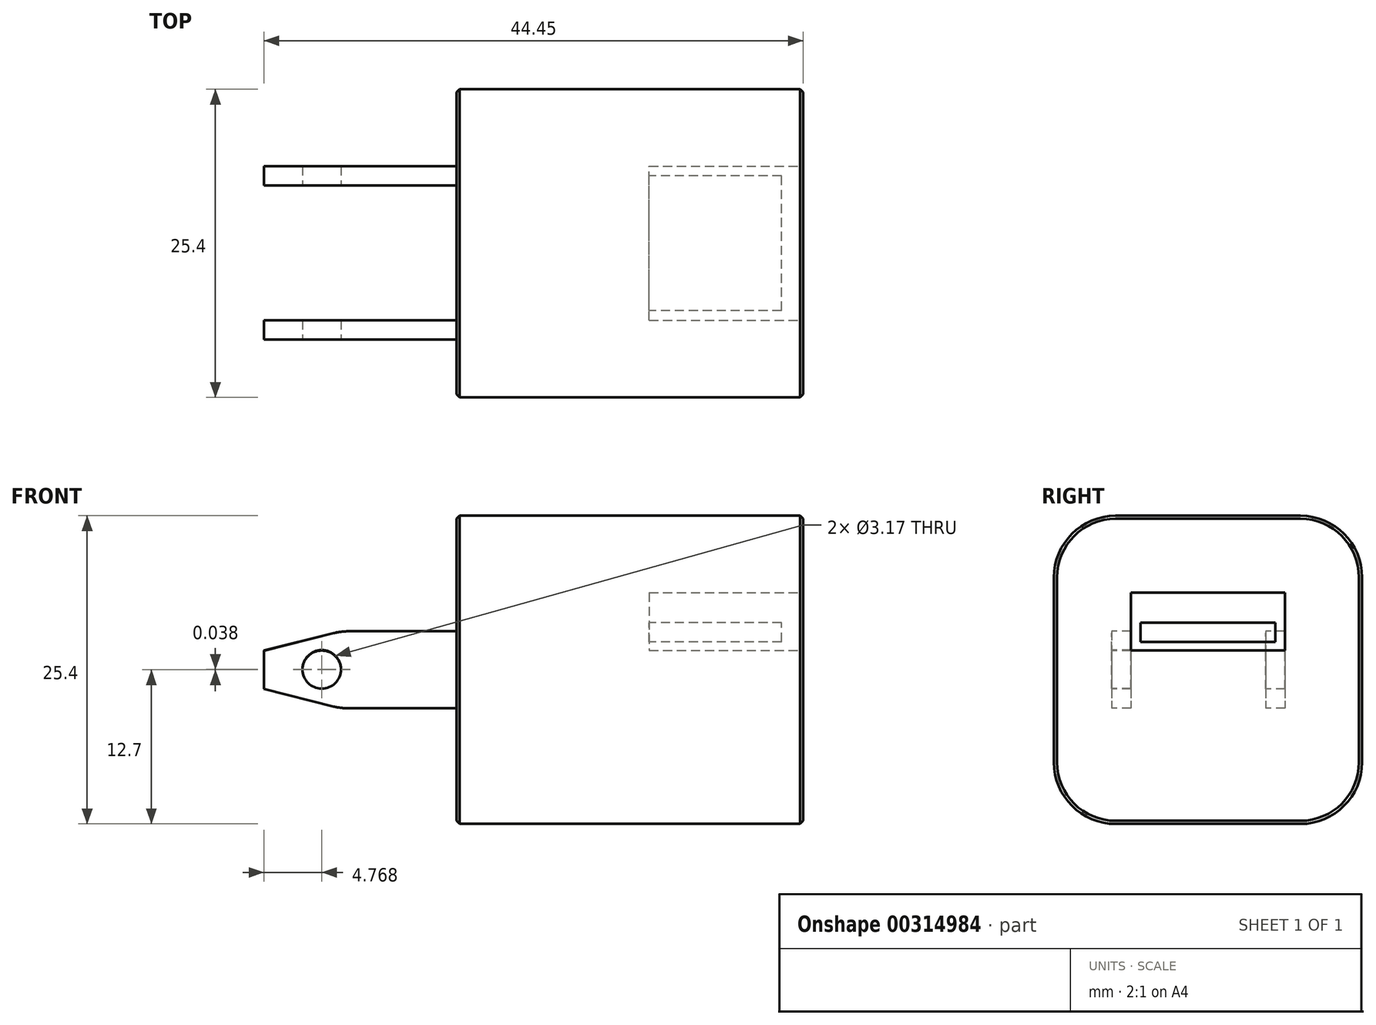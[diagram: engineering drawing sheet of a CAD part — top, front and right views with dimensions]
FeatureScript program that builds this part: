
annotation { "Feature Type Name" : "Feature", "Feature Type Description" : "" }
export const myFeature = defineFeature(function(context is Context, id is Id, definition is map)
    precondition{}
    {
        {
            var Q0;
            Q0=qCreatedBy(makeId("Top.planeOp"),FACE);
            var sketch = newSketch(context, id + "F0", { "sketchPlane" : qUnion([Q0])});
            skLineSegment(sketch, "E0", {"start": v(0, 0) * mm, "end": v(28.58, 0) * mm});
            skLineSegment(sketch, "E1", {"start": v(28.58, 0) * mm, "end": v(28.58, -25.4) * mm});
            skLineSegment(sketch, "E2", {"start": v(0, 0) * mm, "end": v(0, -25.4) * mm});
            skLineSegment(sketch, "E3", {"start": v(0, -25.4) * mm, "end": v(28.58, -25.4) * mm});
            skSolve(sketch);
        }
        {
            var Q0;
            Q0=makeQuery(id+"F0.imprint","IMPRINT",FACE,{"disambiguationData":[TD([[makeQuery(id+"F0.imprint","IMPRINT",EDGE,{"derivedFrom":sQuery(id+"F0.wireOp",EDGE,"E0")}),-1.0]])]});
            extrude(context, id + "F1", {"entities" : qUnion([Q0]), "depth" : 25.4 * mm});
        }
        {
            var Q0;
            Q0=makeQuery(id+"F1.opExtrude","CAP_EDGE",EDGE,{"disambiguationData":[OSD([sQuery(id+"F0.wireOp",EDGE,"E3")])],"isStart":false});
            var Q1;
            Q1=makeQuery(id+"F1.opExtrude","CAP_EDGE",EDGE,{"disambiguationData":[OSD([sQuery(id+"F0.wireOp",EDGE,"E0")])],"isStart":false});
            var Q2;
            Q2=makeQuery(id+"F1.opExtrude","CAP_EDGE",EDGE,{"disambiguationData":[OSD([sQuery(id+"F0.wireOp",EDGE,"E3")])],"isStart":true});
            var Q3;
            Q3=makeQuery(id+"F1.opExtrude","CAP_EDGE",EDGE,{"disambiguationData":[OSD([sQuery(id+"F0.wireOp",EDGE,"E0")])],"isStart":true});
            fillet(context, id + "F2", {"entities" : qUnion([Q0, Q1, Q2, Q3]), "radius" : 5.08 * mm, "tangentPropagation" : true, "allowEdgeOverflow" : false});
        }
        {
            var Q0;
            Q0=makeQuery(id+"F1.opExtrude","SWEPT_FACE",FACE,{"disambiguationData":[OSD([sQuery(id+"F0.wireOp",EDGE,"E1")])]});
            var sketch = newSketch(context, id + "F3", { "sketchPlane" : qUnion([Q0])});
            skLineSegment(sketch, "E4", {"start": v(-19.05, 19.05) * mm, "end": v(-6.35, 19.05) * mm});
            skLineSegment(sketch, "E5", {"start": v(-19.05, 19.05) * mm, "end": v(-19.05, 14.29) * mm});
            skLineSegment(sketch, "E6", {"start": v(-19.05, 14.29) * mm, "end": v(-6.35, 14.29) * mm});
            skLineSegment(sketch, "E7", {"start": v(-6.35, 14.29) * mm, "end": v(-6.35, 19.05) * mm});
            skSolve(sketch);
        }
        {
            var Q0;
            Q0 = qSketchRegion(id + "F3", true);
            extrude(context, id + "F4", {"entities" : qUnion([Q0]), "operationType" : NewBodyOperationType.REMOVE, "oppositeDirection" : true, "depth" : 12.7 * mm});
        }
        {
            var Q0;
            Q0=makeQuery(id+"F4.boolean.opBoolean","COPY",FACE,{"derivedFrom":makeQuery(id+"F4.opExtrude","CAP_FACE",FACE,{"disambiguationData":[OSD([sQuery(id+"F3.wireOp",EDGE,"E4"),sQuery(id+"F3.wireOp",EDGE,"E5"),sQuery(id+"F3.wireOp",EDGE,"E6"),sQuery(id+"F3.wireOp",EDGE,"E7")])],"isStart":false})});
            var sketch = newSketch(context, id + "F5", { "sketchPlane" : qUnion([Q0])});
            skLineSegment(sketch, "E8", {"start": v(-18.25, 15.01) * mm, "end": v(-7.14, 15.01) * mm});
            skLineSegment(sketch, "E9", {"start": v(-7.14, 15.01) * mm, "end": v(-7.14, 16.6) * mm});
            skLineSegment(sketch, "E10", {"start": v(-18.25, 15.01) * mm, "end": v(-18.25, 16.6) * mm});
            skLineSegment(sketch, "E11", {"start": v(-18.25, 16.6) * mm, "end": v(-7.14, 16.6) * mm});
            skSolve(sketch);
        }
        {
            var Q0;
            Q0=makeQuery(id+"F5.imprint","IMPRINT",FACE,{"disambiguationData":[TD([[makeQuery(id+"F5.imprint","IMPRINT",EDGE,{"derivedFrom":sQuery(id+"F5.wireOp",EDGE,"E8")}),1.0]])]});
            extrude(context, id + "F6", {"entities" : qUnion([Q0]), "operationType" : NewBodyOperationType.ADD, "depth" : 10.92 * mm});
        }
        {
            var Q0;
            Q0=makeQuery(id+"F1.opExtrude","SWEPT_FACE",FACE,{"disambiguationData":[OSD([sQuery(id+"F0.wireOp",EDGE,"E2")])]});
            var sketch = newSketch(context, id + "F7", { "sketchPlane" : qUnion([Q0])});
            skLineSegment(sketch, "E12", {"start": v(19.05, 15.88) * mm, "end": v(20.64, 15.88) * mm});
            skLineSegment(sketch, "E13", {"start": v(19.05, 15.88) * mm, "end": v(19.05, 9.53) * mm});
            skLineSegment(sketch, "E14", {"start": v(19.05, 9.53) * mm, "end": v(20.64, 9.53) * mm});
            skLineSegment(sketch, "E15", {"start": v(20.64, 15.88) * mm, "end": v(20.64, 9.53) * mm});
            skSolve(sketch);
        }
        {
            var Q0;
            Q0=makeQuery(id+"F7.imprint","IMPRINT",FACE,{"disambiguationData":[TD([[makeQuery(id+"F7.imprint","IMPRINT",EDGE,{"derivedFrom":sQuery(id+"F7.wireOp",EDGE,"E12")}),-1.0]])]});
            extrude(context, id + "F8", {"entities" : qUnion([Q0]), "operationType" : NewBodyOperationType.ADD, "depth" : 9.52 * mm});
        }
        {
            var Q0;
            Q0=makeQuery(id+"F8.opExtrude","SWEPT_FACE",FACE,{"disambiguationData":[OSD([sQuery(id+"F7.wireOp",EDGE,"E15")])]});
            var sketch = newSketch(context, id + "F9", { "sketchPlane" : qUnion([Q0])});
            skLineSegment(sketch, "E16", {"start": v(-9.53, 9.53) * mm, "end": v(-9.53, 11.11) * mm});
            skLineSegment(sketch, "E17", {"start": v(-9.53, 11.11) * mm, "end": v(-15.88, 11.11) * mm});
            skLineSegment(sketch, "E18", {"start": v(-15.88, 11.11) * mm, "end": v(-9.53, 9.53) * mm});
            skLineSegment(sketch, "E19", {"start": v(-9.53, 15.88) * mm, "end": v(-9.53, 14.27) * mm});
            skLineSegment(sketch, "E20", {"start": v(-9.53, 14.27) * mm, "end": v(-15.88, 14.27) * mm});
            skLineSegment(sketch, "E21", {"start": v(-15.88, 14.27) * mm, "end": v(-9.53, 15.88) * mm});
            skLineSegment(sketch, "E22", {"start": v(-15.88, 14.27) * mm, "end": v(-15.88, 11.11) * mm});
            skLineSegment(sketch, "E23", {"start": v(-9.53, 14.27) * mm, "end": v(-9.53, 11.11) * mm});
            skSolve(sketch);
        }
        {
            var Q0;
            Q0 = qSketchRegion(id + "F9", true);
            extrude(context, id + "F10", {"entities" : qUnion([Q0]), "operationType" : NewBodyOperationType.ADD, "oppositeDirection" : true, "depth" : 1.59 * mm});
        }
        {
            var Q0;
            Q0=makeQuery(id+"F10.boolean.opBoolean","MERGE",FACE,{"derivedFrom":[makeQuery(id+"F8.opExtrude","SWEPT_FACE",FACE,{"disambiguationData":[OSD([sQuery(id+"F7.wireOp",EDGE,"E15")])]}),makeQuery(id+"F10.opExtrude","CAP_FACE",FACE,{"disambiguationData":[OSD([sQuery(id+"F9.wireOp",EDGE,"E16"),sQuery(id+"F9.wireOp",EDGE,"E18"),sQuery(id+"F9.wireOp",EDGE,"E19"),sQuery(id+"F9.wireOp",EDGE,"E21"),sQuery(id+"F9.wireOp",EDGE,"E22"),sQuery(id+"F9.wireOp",EDGE,"E23")])],"isStart":true})]});
            var sketch = newSketch(context, id + "F11", { "sketchPlane" : qUnion([Q0])});
            skCircle(sketch, "E24", {"center": v(-11.11, 12.74) * mm, "radius": 1.59 * mm});
            skSolve(sketch);
        }
        {
            var Q0;
            Q0=makeQuery(id+"F11.imprint","IMPRINT",FACE,{"disambiguationData":[TD([[makeQuery(id+"F11.imprint","IMPRINT",EDGE,{"derivedFrom":sQuery(id+"F11.wireOp",EDGE,"E24")}),1.0]])]});
            extrude(context, id + "F12", {"entities" : qUnion([Q0]), "operationType" : NewBodyOperationType.REMOVE, "oppositeDirection" : true, "depth" : 1.59 * mm});
        }
        {
            var Q0;
            {var subQ0=sQuery(id+"F7.wireOp",EDGE,"E12");Q0=makeQuery(id+"F10.boolean.opBoolean","MERGE",EDGE,{"derivedFrom":[makeQuery(id+"F8.opExtrude","CAP_EDGE",EDGE,{"disambiguationData":[OSD([subQ0])],"isStart":false}),makeQuery(id+"F10.opExtrude","SWEPT_EDGE",EDGE,{"disambiguationData":[OSD([subQ0,sQuery(id+"F7.wireOp",EDGE,"E15"),sQuery(id+"F9.wireOp",EDGE,"E19"),sQuery(id+"F9.wireOp",EDGE,"E21")])]})]});}
            var Q1;
            {var subQ0=sQuery(id+"F7.wireOp",EDGE,"E14");Q1=makeQuery(id+"F10.boolean.opBoolean","MERGE",EDGE,{"derivedFrom":[makeQuery(id+"F8.opExtrude","CAP_EDGE",EDGE,{"disambiguationData":[OSD([subQ0])],"isStart":false}),makeQuery(id+"F10.opExtrude","SWEPT_EDGE",EDGE,{"disambiguationData":[OSD([subQ0,sQuery(id+"F7.wireOp",EDGE,"E15"),sQuery(id+"F9.wireOp",EDGE,"E16"),sQuery(id+"F9.wireOp",EDGE,"E18")])]})]});}
            fillet(context, id + "F13", {"entities" : qUnion([Q0, Q1]), "radius" : 5.08 * mm, "tangentPropagation" : true, "allowEdgeOverflow" : false});
        }
        {
            var Q0;
            Q0=makeQuery(id+"F1.opExtrude","SWEPT_FACE",FACE,{"disambiguationData":[OSD([sQuery(id+"F0.wireOp",EDGE,"E2")])]});
            var sketch = newSketch(context, id + "F14", { "sketchPlane" : qUnion([Q0])});
            skLineSegment(sketch, "E25", {"start": v(6.35, 15.88) * mm, "end": v(7.94, 15.88) * mm});
            skLineSegment(sketch, "E26", {"start": v(6.35, 9.53) * mm, "end": v(7.94, 9.53) * mm});
            skLineSegment(sketch, "E27", {"start": v(6.35, 15.88) * mm, "end": v(6.35, 9.53) * mm});
            skLineSegment(sketch, "E28", {"start": v(7.94, 15.88) * mm, "end": v(7.94, 9.53) * mm});
            skSolve(sketch);
        }
        {
            var Q0;
            Q0=makeQuery(id+"F14.imprint","IMPRINT",FACE,{"disambiguationData":[TD([[makeQuery(id+"F14.imprint","IMPRINT",EDGE,{"derivedFrom":sQuery(id+"F14.wireOp",EDGE,"E25")}),-1.0]])]});
            extrude(context, id + "F15", {"entities" : qUnion([Q0]), "operationType" : NewBodyOperationType.ADD, "depth" : 9.52 * mm});
        }
        {
            var Q0;
            Q0=makeQuery(id+"F15.opExtrude","SWEPT_FACE",FACE,{"disambiguationData":[OSD([sQuery(id+"F14.wireOp",EDGE,"E28")])]});
            var sketch = newSketch(context, id + "F16", { "sketchPlane" : qUnion([Q0])});
            skLineSegment(sketch, "E29", {"start": v(-9.53, 15.88) * mm, "end": v(-9.53, 14.29) * mm});
            skLineSegment(sketch, "E30", {"start": v(-9.53, 14.29) * mm, "end": v(-15.88, 14.29) * mm});
            skLineSegment(sketch, "E31", {"start": v(-15.88, 14.29) * mm, "end": v(-9.53, 15.88) * mm});
            skLineSegment(sketch, "E32", {"start": v(-9.53, 9.53) * mm, "end": v(-9.53, 11.11) * mm});
            skLineSegment(sketch, "E33", {"start": v(-9.53, 11.11) * mm, "end": v(-15.88, 11.11) * mm});
            skLineSegment(sketch, "E34", {"start": v(-15.88, 11.11) * mm, "end": v(-9.53, 9.53) * mm});
            skLineSegment(sketch, "E35", {"start": v(-15.88, 14.29) * mm, "end": v(-15.88, 11.11) * mm});
            skSolve(sketch);
        }
        {
            var Q0;
            {var subQ0=sQuery(id+"F16.wireOp",EDGE,"E30");Q0=makeQuery(id+"F16.imprint","IMPRINT",FACE,{"disambiguationData":[TD([[makeQuery(id+"F16.imprint","IMPRINT",EDGE,{"derivedFrom":subQ0}),1.0]])]});}
            var Q1;
            Q1=makeQuery(id+"F16.imprint","IMPRINT",FACE,{"disambiguationData":[TD([[makeQuery(id+"F16.imprint","IMPRINT",EDGE,{"derivedFrom":sQuery(id+"F16.wireOp",EDGE,"E29")}),-1.0]])]});
            var Q2;
            Q2=makeQuery(id+"F16.imprint","IMPRINT",FACE,{"disambiguationData":[TD([[makeQuery(id+"F16.imprint","IMPRINT",EDGE,{"derivedFrom":sQuery(id+"F16.wireOp",EDGE,"E32")}),-1.0]])]});
            extrude(context, id + "F17", {"entities" : qUnion([Q0, Q1, Q2]), "operationType" : NewBodyOperationType.ADD, "oppositeDirection" : true, "depth" : 1.59 * mm});
        }
        {
            var Q0;
            {var subQ0=sQuery(id+"F14.wireOp",EDGE,"E28");Q0=makeQuery(id+"F17.boolean.opBoolean","MERGE",FACE,{"derivedFrom":[makeQuery(id+"F15.opExtrude","SWEPT_FACE",FACE,{"disambiguationData":[OSD([subQ0])]}),makeQuery(id+"F17.opExtrude","CAP_FACE",FACE,{"disambiguationData":[OSD([subQ0,sQuery(id+"F16.wireOp",EDGE,"E29"),sQuery(id+"F16.wireOp",EDGE,"E31"),sQuery(id+"F16.wireOp",EDGE,"E32"),sQuery(id+"F16.wireOp",EDGE,"E34"),sQuery(id+"F16.wireOp",EDGE,"E35")])],"isStart":true})]});}
            var sketch = newSketch(context, id + "F18", { "sketchPlane" : qUnion([Q0])});
            skCircle(sketch, "E36", {"center": v(-11.11, 12.7) * mm, "radius": 1.59 * mm});
            skSolve(sketch);
        }
        {
            var Q0;
            Q0=makeQuery(id+"F18.imprint","IMPRINT",FACE,{"disambiguationData":[TD([[makeQuery(id+"F18.imprint","IMPRINT",EDGE,{"derivedFrom":sQuery(id+"F18.wireOp",EDGE,"E36")}),1.0]])]});
            extrude(context, id + "F19", {"entities" : qUnion([Q0]), "operationType" : NewBodyOperationType.REMOVE, "oppositeDirection" : true, "depth" : 1.59 * mm});
        }
        {
            var Q0;
            {var subQ0=sQuery(id+"F14.wireOp",EDGE,"E25");Q0=makeQuery(id+"F17.boolean.opBoolean","MERGE",EDGE,{"derivedFrom":[makeQuery(id+"F15.opExtrude","CAP_EDGE",EDGE,{"disambiguationData":[OSD([subQ0])],"isStart":false}),makeQuery(id+"F17.opExtrude","SWEPT_EDGE",EDGE,{"disambiguationData":[OSD([subQ0,sQuery(id+"F14.wireOp",EDGE,"E28"),sQuery(id+"F16.wireOp",EDGE,"E29"),sQuery(id+"F16.wireOp",EDGE,"E31")])]})]});}
            var Q1;
            {var subQ0=sQuery(id+"F14.wireOp",EDGE,"E26");Q1=makeQuery(id+"F17.boolean.opBoolean","MERGE",EDGE,{"derivedFrom":[makeQuery(id+"F15.opExtrude","CAP_EDGE",EDGE,{"disambiguationData":[OSD([subQ0])],"isStart":false}),makeQuery(id+"F17.opExtrude","SWEPT_EDGE",EDGE,{"disambiguationData":[OSD([subQ0,sQuery(id+"F14.wireOp",EDGE,"E28"),sQuery(id+"F16.wireOp",EDGE,"E32"),sQuery(id+"F16.wireOp",EDGE,"E34")])]})]});}
            fillet(context, id + "F20", {"entities" : qUnion([Q0, Q1]), "radius" : 5.08 * mm, "tangentPropagation" : true, "allowEdgeOverflow" : false});
        }
        {
            var Q0;
            Q0=makeQuery(id+"F1.opExtrude","CAP_EDGE",EDGE,{"disambiguationData":[OSD([sQuery(id+"F0.wireOp",EDGE,"E1")])],"isStart":false});
            chamfer(context, id + "F21", {"entities" : qUnion([Q0]), "width" : 0.25 * mm, "tangentPropagation" : true});
        }
        {
            var Q0;
            Q0=makeQuery(id+"F1.opExtrude","CAP_EDGE",EDGE,{"disambiguationData":[OSD([sQuery(id+"F0.wireOp",EDGE,"E2")])],"isStart":false});
            chamfer(context, id + "F22", {"entities" : qUnion([Q0]), "width" : 0.25 * mm, "tangentPropagation" : true});
        }
    });
